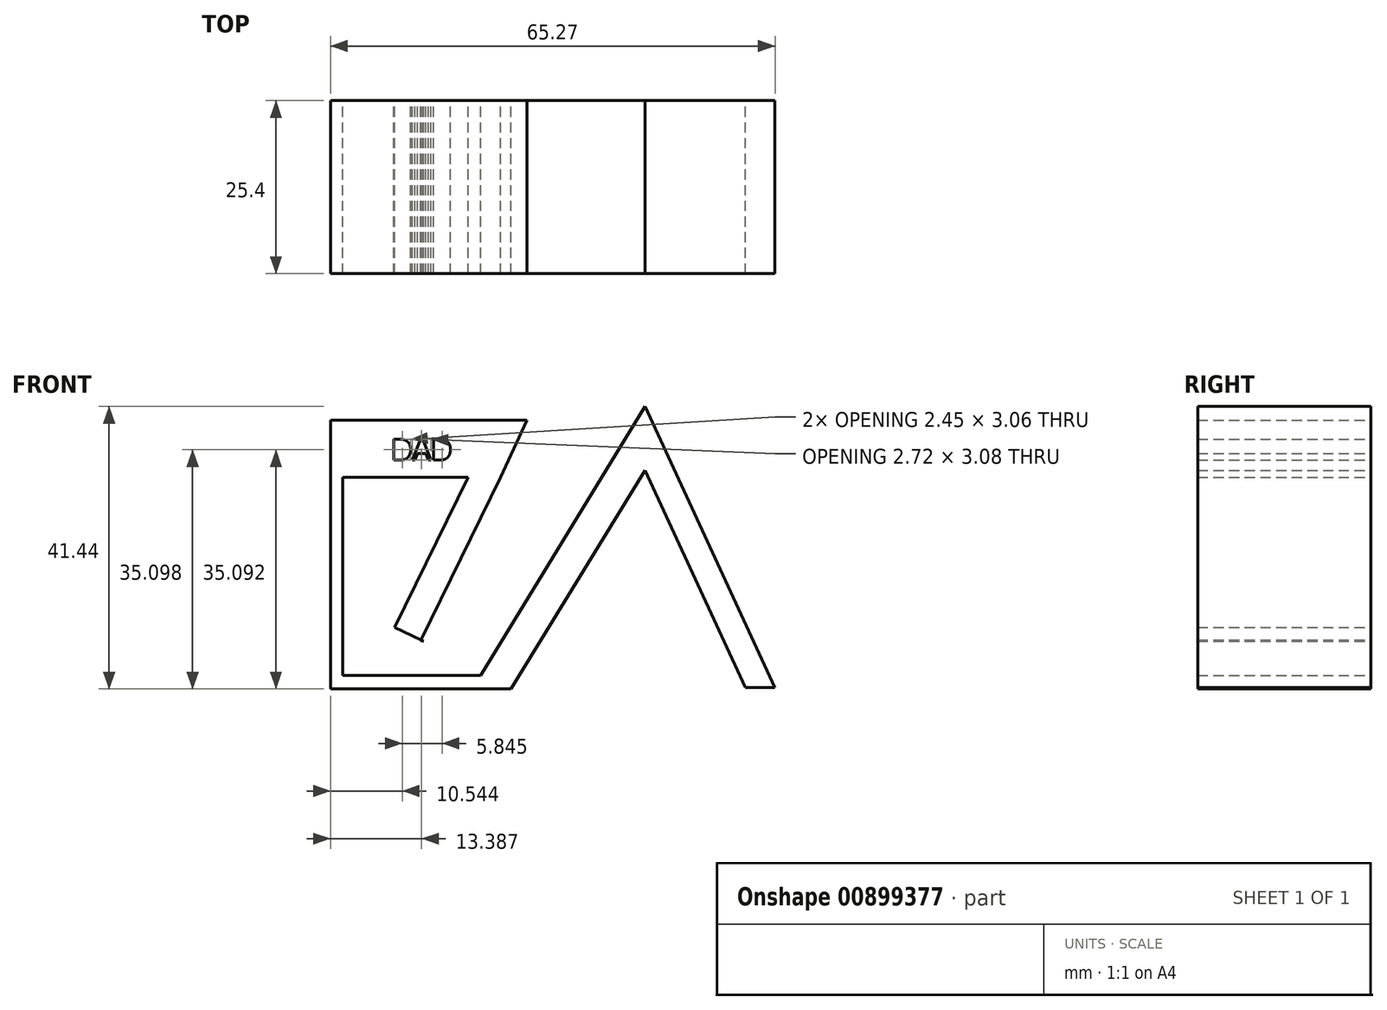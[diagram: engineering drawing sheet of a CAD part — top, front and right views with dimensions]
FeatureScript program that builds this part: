
annotation { "Feature Type Name" : "Feature", "Feature Type Description" : "" }
export const myFeature = defineFeature(function(context is Context, id is Id, definition is map)
    precondition{}
    {
        {
            var Q0;
            Q0=qCreatedBy(makeId("Front.planeOp"),FACE);
            var sketch = newSketch(context, id + "F0", { "sketchPlane" : qUnion([Q0])});
            skLineSegment(sketch, "E0", {"start": v(5.2, 21.18) * mm, "end": v(19.93, -10.7) * mm});
            skLineSegment(sketch, "E1", {"start": v(24.29, -10.7) * mm, "end": v(5.23, 30.53) * mm});
            skLineSegment(sketch, "E2", {"start": v(5.23, 30.53) * mm, "end": v(-18.95, -8.92) * mm});
            skLineSegment(sketch, "E3", {"start": v(5.2, 21.18) * mm, "end": v(-14.47, -10.91) * mm});
            skLineSegment(sketch, "E4", {"start": v(24.29, -10.7) * mm, "end": v(19.93, -10.7) * mm});
            skLineSegment(sketch, "E5", {"start": v(-18.95, -8.92) * mm, "end": v(-39.18, -8.92) * mm});
            skLineSegment(sketch, "E6", {"start": v(-14.47, -10.91) * mm, "end": v(-40.98, -10.91) * mm});
            skLineSegment(sketch, "E7", {"start": v(-40.98, -8.92) * mm, "end": v(-40.98, -10.91) * mm});
            skLineSegment(sketch, "E8", {"start": v(-40.98, -8.92) * mm, "end": v(-40.98, 28.52) * mm});
            skLineSegment(sketch, "E9", {"start": v(-40.98, 28.52) * mm, "end": v(-32.08, 28.52) * mm});
            skLineSegment(sketch, "E10", {"start": v(-39.18, -8.92) * mm, "end": v(-39.18, 20.16) * mm});
            skLineSegment(sketch, "E11", {"start": v(-39.18, 20.16) * mm, "end": v(-20.77, 20.16) * mm});
            skLineSegment(sketch, "E12", {"start": v(-32.08, 28.52) * mm, "end": v(-12.14, 28.52) * mm});
            skLineSegment(sketch, "E13", {"start": v(-12.14, 28.52) * mm, "end": v(-16, 20.16) * mm});
            skLineSegment(sketch, "E14", {"start": v(-16, 20.16) * mm, "end": v(-27.72, -3.86) * mm});
            skLineSegment(sketch, "E15", {"start": v(-20.77, 20.16) * mm, "end": v(-31.53, -1.9) * mm});
            skLineSegment(sketch, "E16", {"start": v(-27.72, -3.86) * mm, "end": v(-27.32, -3.93) * mm});
            skLineSegment(sketch, "E17", {"start": v(-31.53, -1.9) * mm, "end": v(-27.32, -3.93) * mm});
            skText(sketch, "E18", { "text": "DAD\n", "fontName": "OpenSans-Regular.ttf"});
            const initialGuessF0  = {"E18": [-0.03208, 0.02265, 1, 0, 0.00309]};
            skSetInitialGuess(sketch, initialGuessF0);
            skSolve(sketch);
        }
        {
            var Q0;
            Q0 = qSketchRegion(id + "F0", true);
            extrude(context, id + "F1", {"entities" : qUnion([Q0]), "depth" : 25.4 * mm, "offsetDistance" : 25.4 * mm});
        }
    });
